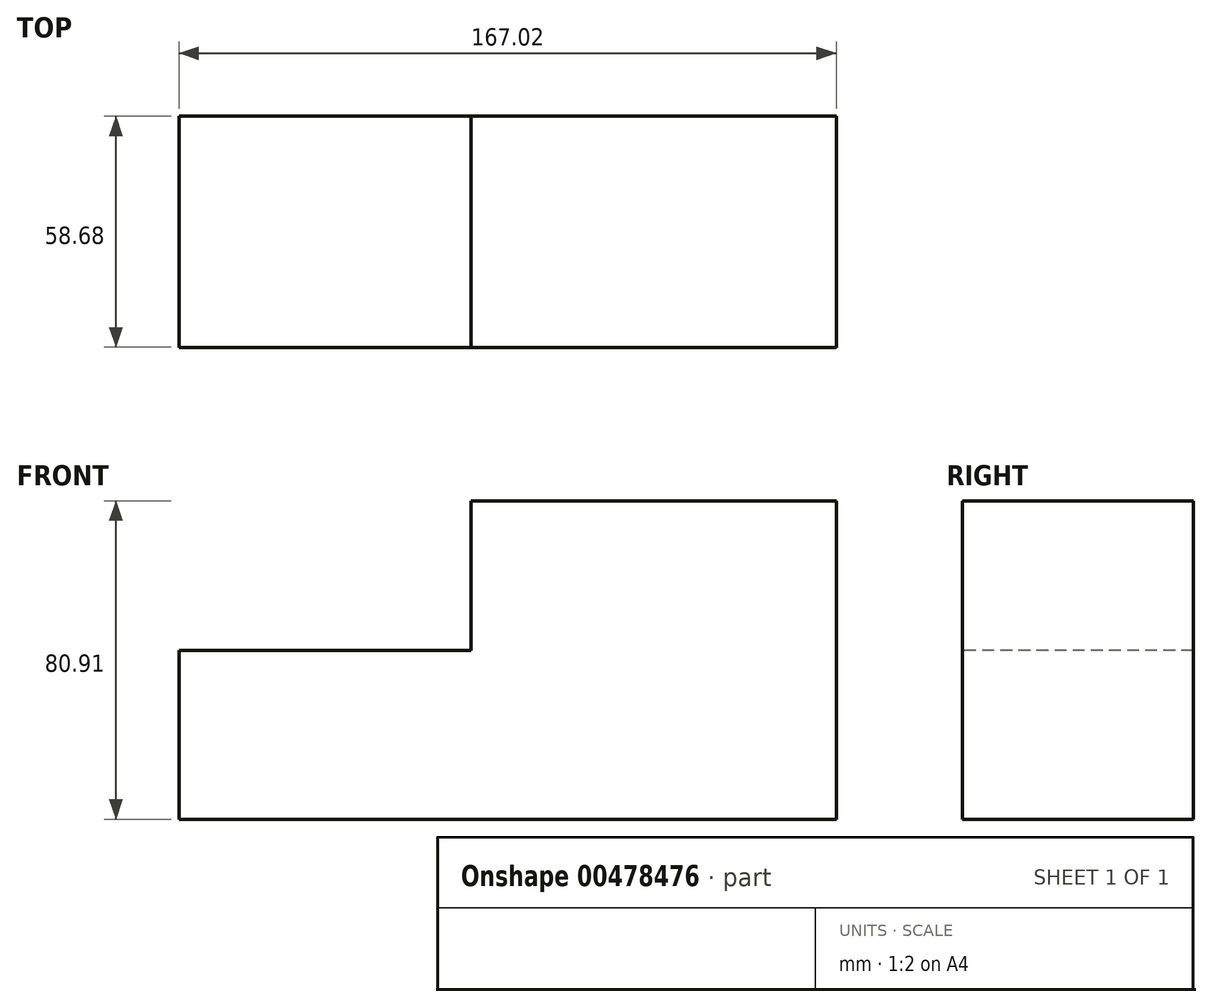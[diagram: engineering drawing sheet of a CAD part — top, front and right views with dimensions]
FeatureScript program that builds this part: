
annotation { "Feature Type Name" : "Feature", "Feature Type Description" : "" }
export const myFeature = defineFeature(function(context is Context, id is Id, definition is map)
    precondition{}
    {
        {
            var Q0;
            Q0=qCreatedBy(makeId("Top.planeOp"),FACE);
            var sketch = newSketch(context, id + "F0", { "sketchPlane" : qUnion([Q0])});
            skLineSegment(sketch, "E0.bottom", {"start": v(-74.25, 23.78) * mm, "end": v(92.77, 23.78) * mm});
            skLineSegment(sketch, "E0.top", {"start": v(-74.25, -24.68) * mm, "end": v(92.77, -24.68) * mm});
            skLineSegment(sketch, "E0.left", {"start": v(-74.25, 23.78) * mm, "end": v(-74.25, -24.68) * mm});
            skLineSegment(sketch, "E0.right", {"start": v(92.77, 23.78) * mm, "end": v(92.77, -24.68) * mm});
            skSolve(sketch);
        }
        {
            var Q0;
            Q0=makeQuery(id+"F0.imprint","IMPRINT",FACE,{"disambiguationData":[TD([[makeQuery(id+"F0.imprint","IMPRINT",EDGE,{"derivedFrom":sQuery(id+"F0.wireOp",EDGE,"E0.bottom")}),-1.0]])]});
            extrude(context, id + "F1", {"entities" : qUnion([Q0]), "depth" : 42.84 * mm});
        }
        {
            var Q0;
            Q0=makeQuery(id+"F1.opExtrude","SWEPT_FACE",FACE,{"disambiguationData":[OSD([sQuery(id+"F0.wireOp",EDGE,"E0.top")])]});
            extrude(context, id + "F2", {"entities" : qUnion([Q0]), "operationType" : NewBodyOperationType.ADD, "depth" : 10.23 * mm});
        }
        {
            var Q0;
            {var subQ0=sQuery(id+"F0.wireOp",EDGE,"E0.top");Q0=makeQuery(id+"F2.boolean.opBoolean","MERGE",FACE,{"derivedFrom":[makeQuery(id+"F1.opExtrude","CAP_FACE",FACE,{"disambiguationData":[OSD([sQuery(id+"F0.wireOp",EDGE,"E0.bottom"),subQ0,sQuery(id+"F0.wireOp",EDGE,"E0.left"),sQuery(id+"F0.wireOp",EDGE,"E0.right")])],"isStart":false}),makeQuery(id+"F2.opExtrude","SWEPT_FACE",FACE,{"disambiguationData":[OSD([subQ0]),TDD([makeQuery(id+"F1.opExtrude","CAP_EDGE",EDGE,{"disambiguationData":[OSD([subQ0])],"isStart":false})])]})]});}
            var sketch = newSketch(context, id + "F3", { "sketchPlane" : qUnion([Q0])});
            skPoint(sketch, "E1.firstSnap0", {"position": v(9.26, 23.78) * mm});
            skLineSegment(sketch, "E1.bottom", {"start": v(0, 23.78) * mm, "end": v(92.77, 23.78) * mm});
            skLineSegment(sketch, "E1.top", {"start": v(0, -34.9) * mm, "end": v(92.77, -34.9) * mm});
            skLineSegment(sketch, "E1.left", {"start": v(0, 23.78) * mm, "end": v(0, -34.9) * mm});
            skLineSegment(sketch, "E1.right", {"start": v(92.77, 23.78) * mm, "end": v(92.77, -34.9) * mm});
            skSolve(sketch);
        }
        {
            var Q0;
            Q0=makeQuery(id+"F3.imprint","IMPRINT",FACE,{"disambiguationData":[TD([[makeQuery(id+"F3.imprint","IMPRINT",EDGE,{"derivedFrom":sQuery(id+"F3.wireOp",EDGE,"E1.bottom")}),-1.0]])]});
            extrude(context, id + "F4", {"entities" : qUnion([Q0]), "operationType" : NewBodyOperationType.ADD, "depth" : 38.06 * mm});
        }
    });
